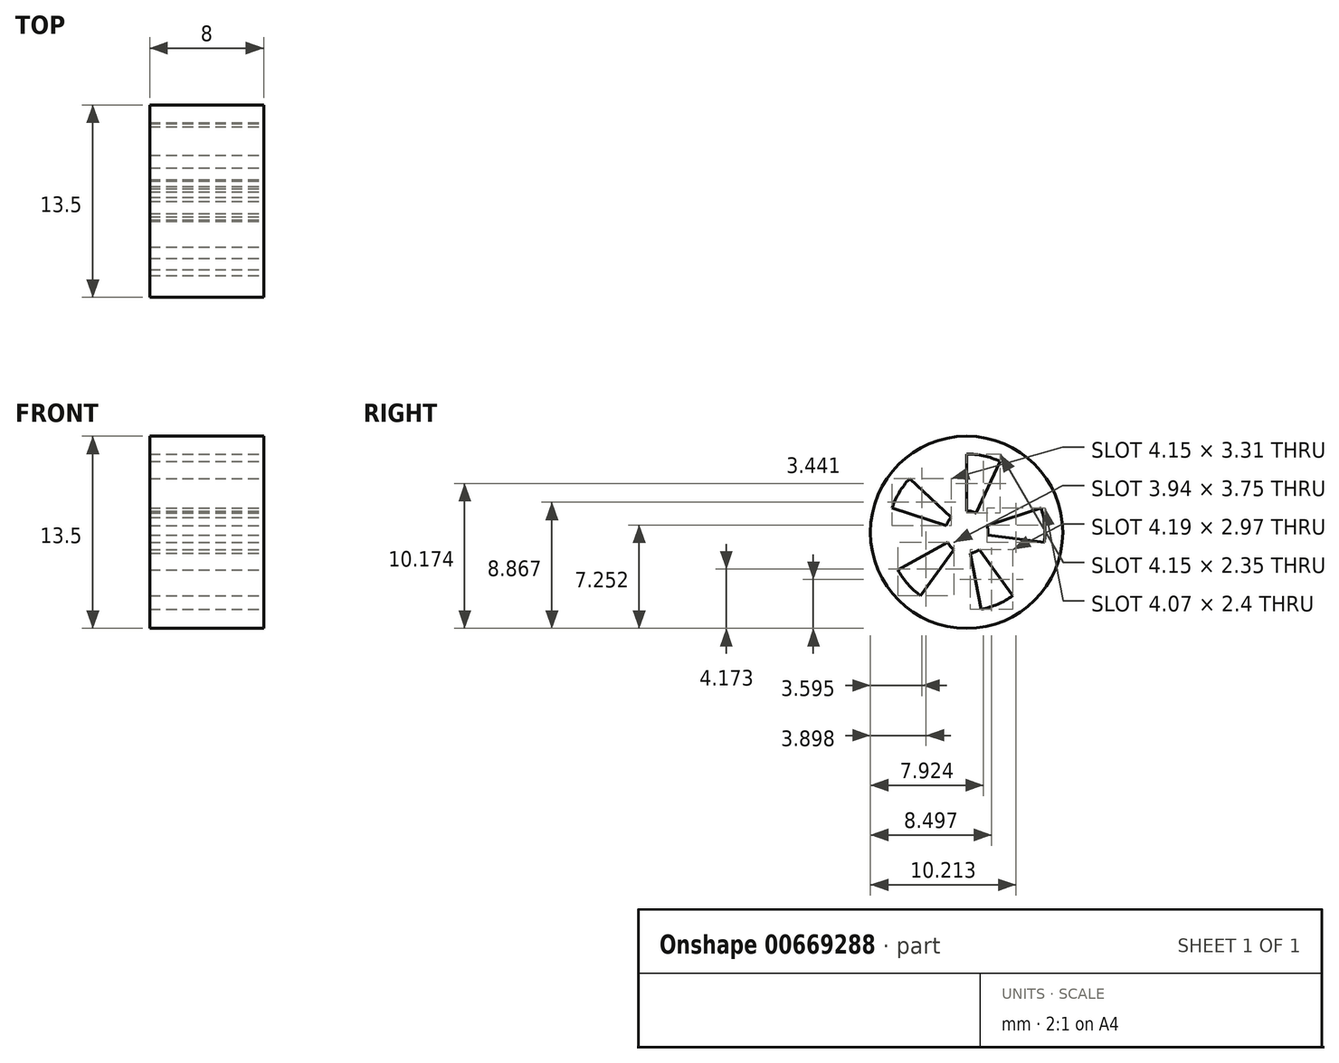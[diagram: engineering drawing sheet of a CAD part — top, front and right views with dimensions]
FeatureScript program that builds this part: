
annotation { "Feature Type Name" : "Feature", "Feature Type Description" : "" }
export const myFeature = defineFeature(function(context is Context, id is Id, definition is map)
    precondition{}
    {
        {
            var Q0;
            Q0=qCreatedBy(makeId("Right.planeOp"),FACE);
            var sketch = newSketch(context, id + "F0", { "sketchPlane" : qUnion([Q0])});
            skCircle(sketch, "E0", {"center": v(0, 0) * mm, "radius": 6.75 * mm});
            skSolve(sketch);
        }
        {
            var Q0;
            Q0=makeQuery(id+"F0.imprint","IMPRINT",FACE,{"disambiguationData":[TD([[makeQuery(id+"F0.imprint","IMPRINT",EDGE,{"derivedFrom":sQuery(id+"F0.wireOp",EDGE,"E0")}),1.0]])]});
            extrude(context, id + "F1", {"entities" : qUnion([Q0]), "depth" : 8 * mm, "offsetDistance" : 25 * mm});
        }
        {
            var Q0;
            Q0=makeQuery(id+"F1.opExtrude","CAP_FACE",FACE,{"disambiguationData":[OSD([sQuery(id+"F0.wireOp",EDGE,"E0")])],"isStart":false});
            var sketch = newSketch(context, id + "F2", { "sketchPlane" : qUnion([Q0])});
            skCircle(sketch, "E1", {"center": v(0, 0) * mm, "radius": 5.5 * mm});
            skCircle(sketch, "E2", {"center": v(0, 0) * mm, "radius": 1.5 * mm});
            skLineSegment(sketch, "E3", {"start": v(0, 1.5) * mm, "end": v(0, 5.5) * mm});
            skLineSegment(sketch, "E4", {"start": v(0.66, 1.35) * mm, "end": v(2.35, 4.97) * mm});
            skLineSegment(sketch, "E5.1.0", {"start": v(-1.43, 0.46) * mm, "end": v(-5.23, 1.7) * mm});
            skLineSegment(sketch, "E5.1.1", {"start": v(-1.08, 1.04) * mm, "end": v(-4, 3.77) * mm});
            skLineSegment(sketch, "E5.2.0", {"start": v(-0.88, -1.21) * mm, "end": v(-3.23, -4.45) * mm});
            skLineSegment(sketch, "E5.2.1", {"start": v(-1.32, -0.7) * mm, "end": v(-4.82, -2.64) * mm});
            skLineSegment(sketch, "E5.3.0", {"start": v(0.88, -1.21) * mm, "end": v(3.23, -4.45) * mm});
            skLineSegment(sketch, "E5.3.1", {"start": v(0.26, -1.48) * mm, "end": v(1.02, -5.4) * mm});
            skLineSegment(sketch, "E5.4.0", {"start": v(1.43, 0.46) * mm, "end": v(5.23, 1.7) * mm});
            skLineSegment(sketch, "E5.4.1", {"start": v(1.49, -0.2) * mm, "end": v(5.46, -0.7) * mm});
            skSolve(sketch);
        }
        {
            var Q0;
            {var subQ0=sQuery(id+"F2.wireOp",EDGE,"E5.1.0");Q0=makeQuery(id+"F2.imprint","IMPRINT",FACE,{"disambiguationData":[TD([[makeQuery(id+"F2.imprint","IMPRINT",EDGE,{"derivedFrom":subQ0}),-1.0]])]});}
            var Q1;
            {var subQ0=sQuery(id+"F2.wireOp",EDGE,"E3");Q1=makeQuery(id+"F2.imprint","IMPRINT",FACE,{"disambiguationData":[TD([[makeQuery(id+"F2.imprint","IMPRINT",EDGE,{"derivedFrom":subQ0}),-1.0]])]});}
            var Q2;
            {var subQ0=sQuery(id+"F2.wireOp",EDGE,"E5.4.0");Q2=makeQuery(id+"F2.imprint","IMPRINT",FACE,{"disambiguationData":[TD([[makeQuery(id+"F2.imprint","IMPRINT",EDGE,{"derivedFrom":subQ0}),-1.0]])]});}
            var Q3;
            {var subQ0=sQuery(id+"F2.wireOp",EDGE,"E5.3.0");Q3=makeQuery(id+"F2.imprint","IMPRINT",FACE,{"disambiguationData":[TD([[makeQuery(id+"F2.imprint","IMPRINT",EDGE,{"derivedFrom":subQ0}),-1.0]])]});}
            var Q4;
            {var subQ0=sQuery(id+"F2.wireOp",EDGE,"E5.2.0");Q4=makeQuery(id+"F2.imprint","IMPRINT",FACE,{"disambiguationData":[TD([[makeQuery(id+"F2.imprint","IMPRINT",EDGE,{"derivedFrom":subQ0}),-1.0]])]});}
            extrude(context, id + "F3", {"entities" : qUnion([Q0, Q1, Q2, Q3, Q4]), "operationType" : NewBodyOperationType.REMOVE, "endBound" : BoundingType.THROUGH_ALL, "oppositeDirection" : true, "depth" : 25 * mm, "offsetDistance" : 25 * mm});
        }
    });
